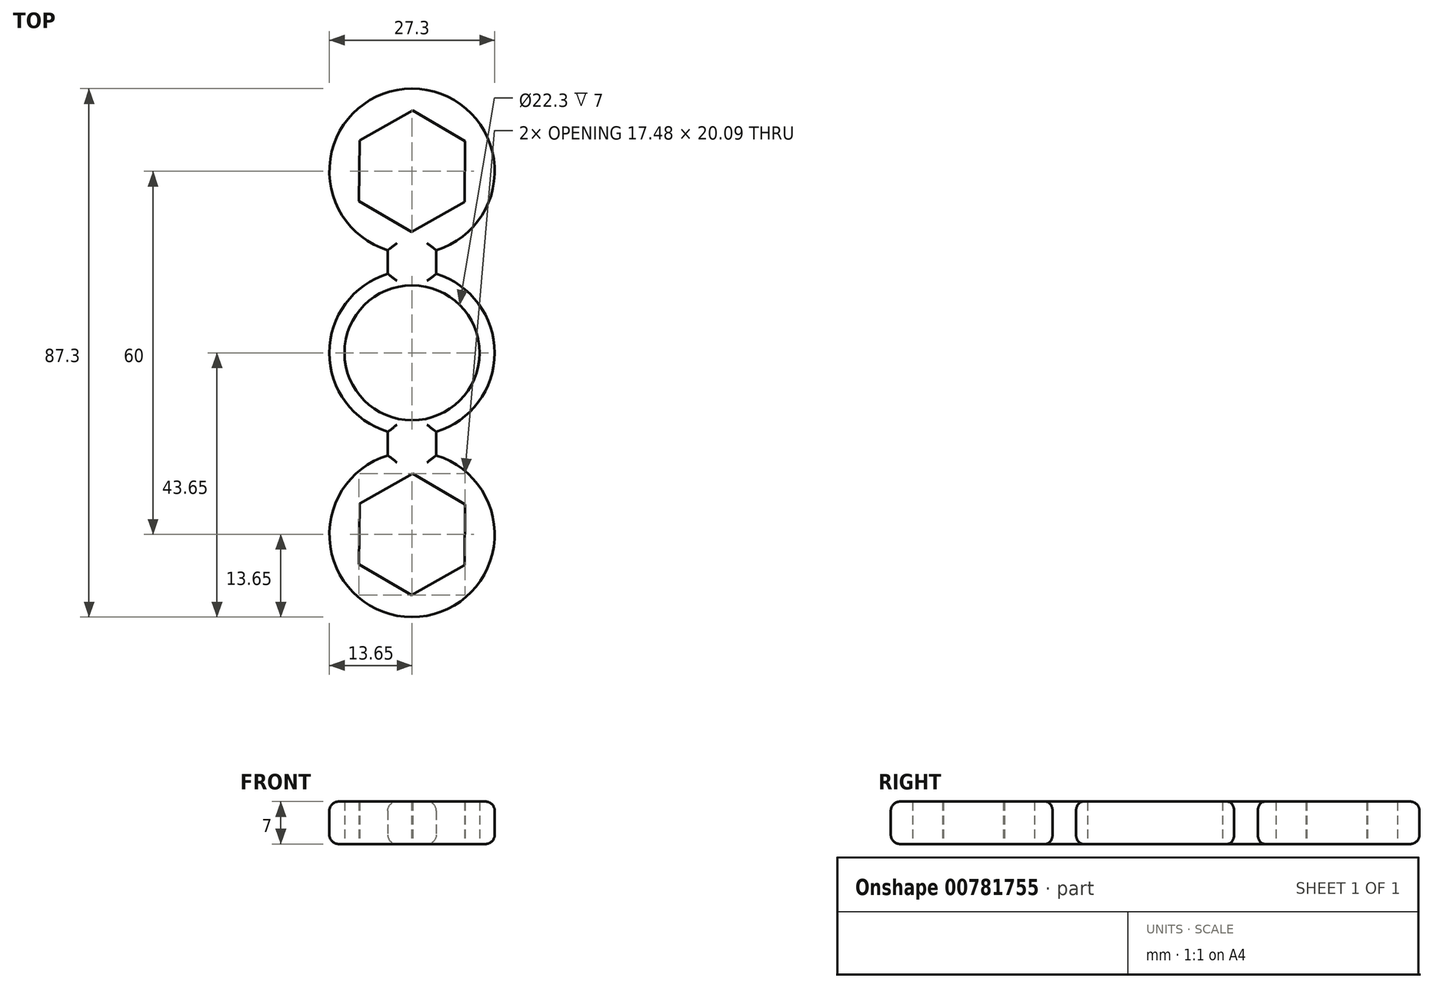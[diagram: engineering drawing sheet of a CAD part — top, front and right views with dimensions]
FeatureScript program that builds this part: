
annotation { "Feature Type Name" : "Feature", "Feature Type Description" : "" }
export const myFeature = defineFeature(function(context is Context, id is Id, definition is map)
    precondition{}
    {
        {
            var Q0;
            Q0=qCreatedBy(makeId("Top.planeOp"),FACE);
            var sketch = newSketch(context, id + "F0", { "sketchPlane" : qUnion([Q0])});
            skCircle(sketch, "E0", {"center": v(0, 0) * mm, "radius": 11.15 * mm});
            skArc(sketch, "E1.0", {"start": v(-4, 13.05) * mm, "mid": v(0, -13.65) * mm, "end": v(4, 13.05) * mm});
            skArc(sketch, "E2.0", {"start": v(4, 16.95) * mm, "mid": v(0, 43.65) * mm, "end": v(-4, 16.95) * mm});
            skLineSegment(sketch, "E3.left", {"start": v(-4, 16.95) * mm, "end": v(-4, 13.05) * mm});
            skLineSegment(sketch, "E3.right", {"start": v(4, 16.95) * mm, "end": v(4, 13.05) * mm});
            skLineSegment(sketch, "E4", {"start": v(0, 0) * mm, "end": v(0, 30) * mm, "construction": true});
            skCircle(sketch, "E5.cCircle", {"center": v(0, 30) * mm, "radius": 8.7 * mm, "construction": true});
            skLineSegment(sketch, "E5.0", {"start": v(8.66, 24.9) * mm, "end": v(-0.08, 19.95) * mm});
            skLineSegment(sketch, "E5.1", {"start": v(-0.08, 19.95) * mm, "end": v(-8.74, 25.05) * mm});
            skLineSegment(sketch, "E5.2", {"start": v(-8.74, 25.05) * mm, "end": v(-8.66, 35.1) * mm});
            skLineSegment(sketch, "E5.3", {"start": v(-8.66, 35.1) * mm, "end": v(0.08, 40.05) * mm});
            skLineSegment(sketch, "E5.4", {"start": v(0.08, 40.05) * mm, "end": v(8.74, 34.95) * mm});
            skLineSegment(sketch, "E5.5", {"start": v(8.74, 34.95) * mm, "end": v(8.66, 24.9) * mm});
            skPoint(sketch, "E5.0.midPoint", {"position": v(4.29, 22.43) * mm});
            skSolve(sketch);
        }
        {
            var Q0;
            Q0=makeQuery(id+"F0.imprint","IMPRINT",FACE,{"disambiguationData":[TD([[makeQuery(id+"F0.imprint","IMPRINT",EDGE,{"derivedFrom":sQuery(id+"F0.wireOp",EDGE,"E0")}),-1.0]])]});
            extrude(context, id + "F1", {"entities" : qUnion([Q0]), "depth" : 7 * mm, "offsetDistance" : 25 * mm});
        }
        {
            var Q0;
            Q0=qCreatedBy(makeId("Front.planeOp"),FACE);
            var sketch = newSketch(context, id + "F2", { "sketchPlane" : qUnion([Q0])});
            skLineSegment(sketch, "E6", {"start": v(0, 0) * mm, "end": v(0, 10.16) * mm, "construction": true});
            skSolve(sketch);
        }
        {
            var Q0;
            Q0=makeQuery(id+"F1.opExtrude","SWEPT_BODY",BODY,{"disambiguationData":[OSD([sQuery(id+"F0.wireOp",EDGE,"E0"),sQuery(id+"F0.wireOp",EDGE,"E1.0"),sQuery(id+"F0.wireOp",EDGE,"E2.0"),sQuery(id+"F0.wireOp",EDGE,"E3.left"),sQuery(id+"F0.wireOp",EDGE,"E3.right"),sQuery(id+"F0.wireOp",EDGE,"E5.0"),sQuery(id+"F0.wireOp",EDGE,"E5.1"),sQuery(id+"F0.wireOp",EDGE,"E5.2"),sQuery(id+"F0.wireOp",EDGE,"E5.3"),sQuery(id+"F0.wireOp",EDGE,"E5.4"),sQuery(id+"F0.wireOp",EDGE,"E5.5")])]});
            var Q1;
            Q1=sQuery(id+"F2.wireOp",EDGE,"E6");
            circularPattern(context, id + "F3", {"entities" : qUnion([Q0]), "axis" : qUnion([Q1]), "angle" : 360 * degree, "instanceCount" : 2, "equalSpace" : true});
        }
        {
            var Q0;
            Q0=makeQuery(id+"F1.opExtrude","SWEPT_BODY",BODY,{"disambiguationData":[OSD([sQuery(id+"F0.wireOp",EDGE,"E0"),sQuery(id+"F0.wireOp",EDGE,"E1.0"),sQuery(id+"F0.wireOp",EDGE,"E2.0"),sQuery(id+"F0.wireOp",EDGE,"E3.left"),sQuery(id+"F0.wireOp",EDGE,"E3.right"),sQuery(id+"F0.wireOp",EDGE,"E5.0"),sQuery(id+"F0.wireOp",EDGE,"E5.1"),sQuery(id+"F0.wireOp",EDGE,"E5.2"),sQuery(id+"F0.wireOp",EDGE,"E5.3"),sQuery(id+"F0.wireOp",EDGE,"E5.4"),sQuery(id+"F0.wireOp",EDGE,"E5.5")])]});
            var Q1;
            Q1=makeQuery(id+"F3.opPattern","COPY",BODY,{"derivedFrom":makeQuery(id+"F1.opExtrude","SWEPT_BODY",BODY,{"disambiguationData":[OSD([sQuery(id+"F0.wireOp",EDGE,"E0"),sQuery(id+"F0.wireOp",EDGE,"E1.0"),sQuery(id+"F0.wireOp",EDGE,"E2.0"),sQuery(id+"F0.wireOp",EDGE,"E3.left"),sQuery(id+"F0.wireOp",EDGE,"E3.right"),sQuery(id+"F0.wireOp",EDGE,"E5.0"),sQuery(id+"F0.wireOp",EDGE,"E5.1"),sQuery(id+"F0.wireOp",EDGE,"E5.2"),sQuery(id+"F0.wireOp",EDGE,"E5.3"),sQuery(id+"F0.wireOp",EDGE,"E5.4"),sQuery(id+"F0.wireOp",EDGE,"E5.5")])]}),"instanceName":"1"});
            booleanBodies(context, id + "F4", {"operationType" : BooleanOperationType.UNION, "tools" : qUnion([Q0, Q1])});
        }
        {
            var Q0;
            Q0=makeQuery(id+"F1.opExtrude","CAP_EDGE",EDGE,{"disambiguationData":[OSD([sQuery(id+"F0.wireOp",EDGE,"E2.0")])],"isStart":false});
            var Q1;
            Q1=makeQuery(id+"F1.opExtrude","CAP_EDGE",EDGE,{"disambiguationData":[OSD([sQuery(id+"F0.wireOp",EDGE,"E3.right")])],"isStart":false});
            var Q2;
            Q2=makeQuery(id+"F1.opExtrude","CAP_EDGE",EDGE,{"disambiguationData":[OSD([sQuery(id+"F0.wireOp",EDGE,"E3.left")])],"isStart":false});
            var Q3;
            {var subQ1=sQuery(id+"F0.wireOp",EDGE,"E3.left");var subQ2=sQuery(id+"F0.wireOp",EDGE,"E1.0");Q3=makeQuery(id+"F4.opBoolean","SPLIT",EDGE,{"disambiguationData":[TD([makeQuery(id+"F1.opExtrude","SWEPT_FACE",FACE,{"disambiguationData":[OSD([subQ1])]})])],"derivedFrom":makeQuery(id+"F1.opExtrude","CAP_EDGE",EDGE,{"disambiguationData":[OSD([subQ2])],"isStart":false})});}
            var Q4;
            {var subQ0=sQuery(id+"F0.wireOp",EDGE,"E3.right");var subQ2=sQuery(id+"F0.wireOp",EDGE,"E1.0");Q4=makeQuery(id+"F4.opBoolean","SPLIT",EDGE,{"disambiguationData":[TD([makeQuery(id+"F1.opExtrude","SWEPT_FACE",FACE,{"disambiguationData":[OSD([subQ0])]})])],"derivedFrom":makeQuery(id+"F1.opExtrude","CAP_EDGE",EDGE,{"disambiguationData":[OSD([subQ2])],"isStart":false})});}
            var Q5;
            Q5=makeQuery(id+"F3.opPattern","COPY",EDGE,{"derivedFrom":makeQuery(id+"F1.opExtrude","CAP_EDGE",EDGE,{"disambiguationData":[OSD([sQuery(id+"F0.wireOp",EDGE,"E3.left")])],"isStart":false}),"instanceName":"1"});
            var Q6;
            Q6=makeQuery(id+"F3.opPattern","COPY",EDGE,{"derivedFrom":makeQuery(id+"F1.opExtrude","CAP_EDGE",EDGE,{"disambiguationData":[OSD([sQuery(id+"F0.wireOp",EDGE,"E3.right")])],"isStart":false}),"instanceName":"1"});
            var Q7;
            Q7=makeQuery(id+"F3.opPattern","COPY",EDGE,{"derivedFrom":makeQuery(id+"F1.opExtrude","CAP_EDGE",EDGE,{"disambiguationData":[OSD([sQuery(id+"F0.wireOp",EDGE,"E2.0")])],"isStart":false}),"instanceName":"1"});
            var Q8;
            Q8=makeQuery(id+"F3.opPattern","COPY",EDGE,{"derivedFrom":makeQuery(id+"F1.opExtrude","CAP_EDGE",EDGE,{"disambiguationData":[OSD([sQuery(id+"F0.wireOp",EDGE,"E2.0")])],"isStart":true}),"instanceName":"1"});
            var Q9;
            {var subQ0=sQuery(id+"F0.wireOp",EDGE,"E3.right");var subQ2=sQuery(id+"F0.wireOp",EDGE,"E1.0");Q9=makeQuery(id+"F4.opBoolean","SPLIT",EDGE,{"disambiguationData":[TD([makeQuery(id+"F1.opExtrude","SWEPT_FACE",FACE,{"disambiguationData":[OSD([subQ0])]})])],"derivedFrom":makeQuery(id+"F1.opExtrude","CAP_EDGE",EDGE,{"disambiguationData":[OSD([subQ2])],"isStart":true})});}
            var Q10;
            Q10=makeQuery(id+"F3.opPattern","COPY",EDGE,{"derivedFrom":makeQuery(id+"F1.opExtrude","CAP_EDGE",EDGE,{"disambiguationData":[OSD([sQuery(id+"F0.wireOp",EDGE,"E3.left")])],"isStart":true}),"instanceName":"1"});
            var Q11;
            Q11=makeQuery(id+"F3.opPattern","COPY",EDGE,{"derivedFrom":makeQuery(id+"F1.opExtrude","CAP_EDGE",EDGE,{"disambiguationData":[OSD([sQuery(id+"F0.wireOp",EDGE,"E3.right")])],"isStart":true}),"instanceName":"1"});
            var Q12;
            {var subQ0=sQuery(id+"F0.wireOp",EDGE,"E3.left");var subQ2=sQuery(id+"F0.wireOp",EDGE,"E1.0");Q12=makeQuery(id+"F4.opBoolean","SPLIT",EDGE,{"disambiguationData":[TD([makeQuery(id+"F1.opExtrude","SWEPT_FACE",FACE,{"disambiguationData":[OSD([subQ0])]})])],"derivedFrom":makeQuery(id+"F1.opExtrude","CAP_EDGE",EDGE,{"disambiguationData":[OSD([subQ2])],"isStart":true})});}
            var Q13;
            Q13=makeQuery(id+"F1.opExtrude","CAP_EDGE",EDGE,{"disambiguationData":[OSD([sQuery(id+"F0.wireOp",EDGE,"E2.0")])],"isStart":true});
            var Q14;
            Q14=makeQuery(id+"F1.opExtrude","CAP_EDGE",EDGE,{"disambiguationData":[OSD([sQuery(id+"F0.wireOp",EDGE,"E3.right")])],"isStart":true});
            var Q15;
            Q15=makeQuery(id+"F1.opExtrude","CAP_EDGE",EDGE,{"disambiguationData":[OSD([sQuery(id+"F0.wireOp",EDGE,"E3.left")])],"isStart":true});
            fillet(context, id + "F5", {"entities" : qUnion([Q0, Q1, Q2, Q3, Q4, Q5, Q6, Q7, Q8, Q9, Q10, Q11, Q12, Q13, Q14, Q15]), "radius" : 1.5 * mm, "tangentPropagation" : true, "allowEdgeOverflow" : false});
        }
    });
